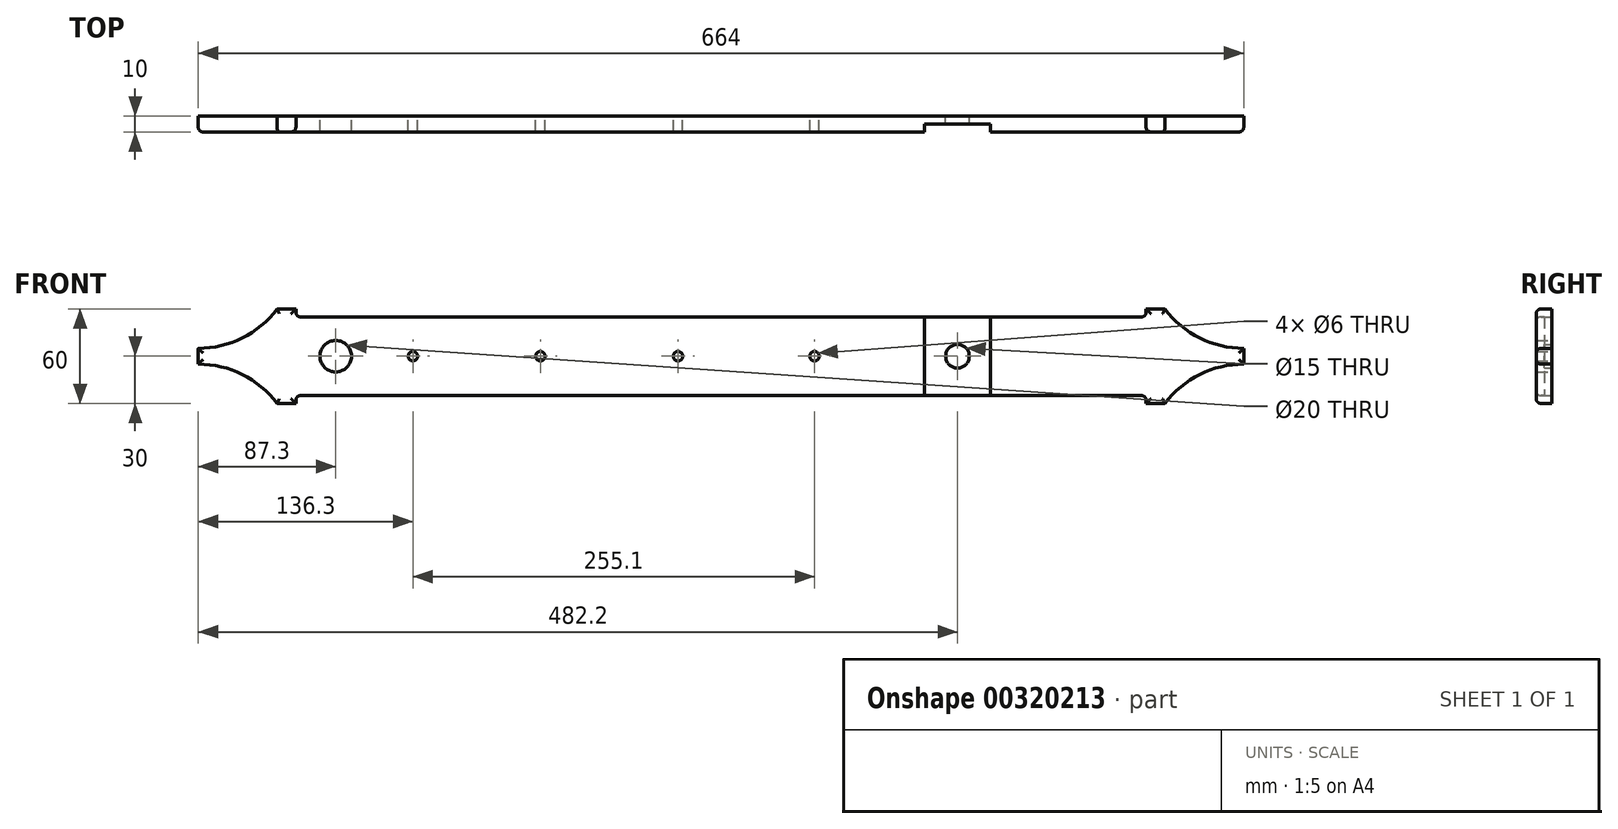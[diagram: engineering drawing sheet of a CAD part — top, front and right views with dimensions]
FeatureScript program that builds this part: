
annotation { "Feature Type Name" : "Feature", "Feature Type Description" : "" }
export const myFeature = defineFeature(function(context is Context, id is Id, definition is map)
    precondition{}
    {
        {
            var Q0;
            Q0=qCreatedBy(makeId("Front.planeOp"),FACE);
            var sketch = newSketch(context, id + "F0", { "sketchPlane" : qUnion([Q0])});
            skLineSegment(sketch, "E0", {"start": v(0, 0) * mm, "end": v(-664, 0) * mm, "construction": true});
            skLineSegment(sketch, "E1", {"start": v(0, 0) * mm, "end": v(0, 5) * mm});
            skLineSegment(sketch, "E2", {"start": v(-50, 30) * mm, "end": v(-62, 30) * mm});
            skArc(sketch, "E3", {"start": v(-50, 30) * mm, "mid": v(-27.95, 11.6) * mm, "end": v(0, 5) * mm});
            skLineSegment(sketch, "E4", {"start": v(-62, 30) * mm, "end": v(-62, 28) * mm});
            skLineSegment(sketch, "E5", {"start": v(-65, 25) * mm, "end": v(-332, 25) * mm});
            skLineSegment(sketch, "E6.MirrorCS", {"start": v(-599, 25) * mm, "end": v(-332, 25) * mm});
            skLineSegment(sketch, "E7.MirrorCS", {"start": v(-602, 30) * mm, "end": v(-602, 28) * mm});
            skLineSegment(sketch, "E8.MirrorCS", {"start": v(-614, 30) * mm, "end": v(-602, 30) * mm});
            skArc(sketch, "E9.MirrorCS", {"start": v(-614, 30) * mm, "mid": v(-636.05, 11.6) * mm, "end": v(-664, 5) * mm});
            skLineSegment(sketch, "E10.MirrorCS", {"start": v(-664, 0) * mm, "end": v(-664, 5) * mm});
            skLineSegment(sketch, "E11.MirrorCS", {"start": v(-664, 0) * mm, "end": v(-664, -5) * mm});
            skArc(sketch, "E12.MirrorCS", {"start": v(-614, -30) * mm, "mid": v(-636.05, -11.6) * mm, "end": v(-664, -5) * mm});
            skLineSegment(sketch, "E13.MirrorCS", {"start": v(-614, -30) * mm, "end": v(-602, -30) * mm});
            skLineSegment(sketch, "E14.MirrorCS", {"start": v(-602, -30) * mm, "end": v(-602, -28) * mm});
            skLineSegment(sketch, "E15.MirrorCS", {"start": v(-599, -25) * mm, "end": v(-332, -25) * mm});
            skLineSegment(sketch, "E16.MirrorCS", {"start": v(-65, -25) * mm, "end": v(-332, -25) * mm});
            skLineSegment(sketch, "E17.MirrorCS", {"start": v(-62, -30) * mm, "end": v(-62, -28) * mm});
            skLineSegment(sketch, "E18.MirrorCS", {"start": v(-50, -30) * mm, "end": v(-62, -30) * mm});
            skArc(sketch, "E19.MirrorCS", {"start": v(-50, -30) * mm, "mid": v(-27.95, -11.6) * mm, "end": v(0, -5) * mm});
            skLineSegment(sketch, "E20.MirrorCS", {"start": v(0, 0) * mm, "end": v(0, -5) * mm});
            skPoint(sketch, "E21.visualSharp", {"position": v(-62, 25) * mm});
            skArc(sketch, "E21.filletArc", {"start": v(-65, 25) * mm, "mid": v(-62.88, 25.88) * mm, "end": v(-62, 28) * mm});
            skPoint(sketch, "E22.visualSharp", {"position": v(-62, -25) * mm});
            skArc(sketch, "E22.filletArc", {"start": v(-62, -28) * mm, "mid": v(-62.88, -25.88) * mm, "end": v(-65, -25) * mm});
            skPoint(sketch, "E23.visualSharp", {"position": v(-602, 25) * mm});
            skArc(sketch, "E23.filletArc", {"start": v(-602, 28) * mm, "mid": v(-601.12, 25.88) * mm, "end": v(-599, 25) * mm});
            skPoint(sketch, "E24.visualSharp", {"position": v(-602, -25) * mm});
            skArc(sketch, "E24.filletArc", {"start": v(-599, -25) * mm, "mid": v(-601.12, -25.88) * mm, "end": v(-602, -28) * mm});
            skCircle(sketch, "E25", {"center": v(-576.7, 0) * mm, "radius": 10 * mm});
            skCircle(sketch, "E26", {"center": v(-527.7, 0) * mm, "radius": 3 * mm});
            skCircle(sketch, "E27", {"center": v(-446.7, 0) * mm, "radius": 3 * mm});
            skCircle(sketch, "E28", {"center": v(-359.3, 0) * mm, "radius": 3 * mm});
            skCircle(sketch, "E29", {"center": v(-272.6, 0) * mm, "radius": 3 * mm});
            skCircle(sketch, "E30", {"center": v(-181.8, 0) * mm, "radius": 7.5 * mm});
            skSolve(sketch);
        }
        {
            var Q0;
            Q0 = qSketchRegion(id + "F0", true);
            extrude(context, id + "F1", {"entities" : qUnion([Q0]), "depth" : 10 * mm});
        }
        {
            var Q0;
            Q0=makeQuery(id+"F1.opExtrude","CAP_FACE",FACE,{"disambiguationData":[OSD([sQuery(id+"F0.wireOp",EDGE,"E2"),sQuery(id+"F0.wireOp",EDGE,"E1"),sQuery(id+"F0.wireOp",EDGE,"E3"),sQuery(id+"F0.wireOp",EDGE,"E4"),sQuery(id+"F0.wireOp",EDGE,"E5"),sQuery(id+"F0.wireOp",EDGE,"E6.MirrorCS"),sQuery(id+"F0.wireOp",EDGE,"E7.MirrorCS"),sQuery(id+"F0.wireOp",EDGE,"E8.MirrorCS"),sQuery(id+"F0.wireOp",EDGE,"E10.MirrorCS"),sQuery(id+"F0.wireOp",EDGE,"E9.MirrorCS"),sQuery(id+"F0.wireOp",EDGE,"E11.MirrorCS"),sQuery(id+"F0.wireOp",EDGE,"E12.MirrorCS"),sQuery(id+"F0.wireOp",EDGE,"E13.MirrorCS"),sQuery(id+"F0.wireOp",EDGE,"E14.MirrorCS"),sQuery(id+"F0.wireOp",EDGE,"E15.MirrorCS"),sQuery(id+"F0.wireOp",EDGE,"E16.MirrorCS"),sQuery(id+"F0.wireOp",EDGE,"E17.MirrorCS"),sQuery(id+"F0.wireOp",EDGE,"E18.MirrorCS"),sQuery(id+"F0.wireOp",EDGE,"E19.MirrorCS"),sQuery(id+"F0.wireOp",EDGE,"E20.MirrorCS"),sQuery(id+"F0.wireOp",EDGE,"E21.filletArc"),sQuery(id+"F0.wireOp",EDGE,"E22.filletArc"),sQuery(id+"F0.wireOp",EDGE,"E23.filletArc"),sQuery(id+"F0.wireOp",EDGE,"E24.filletArc"),sQuery(id+"F0.wireOp",EDGE,"E25"),sQuery(id+"F0.wireOp",EDGE,"E26"),sQuery(id+"F0.wireOp",EDGE,"E27"),sQuery(id+"F0.wireOp",EDGE,"E28"),sQuery(id+"F0.wireOp",EDGE,"E29"),sQuery(id+"F0.wireOp",EDGE,"E30")])],"isStart":false});
            var sketch = newSketch(context, id + "F2", { "sketchPlane" : qUnion([Q0])});
            skLineSegment(sketch, "E31", {"start": v(-160.8, 25) * mm, "end": v(-160.8, -25) * mm});
            skLineSegment(sketch, "E32", {"start": v(-202.8, 25) * mm, "end": v(-202.8, -25) * mm});
            skSolve(sketch);
        }
        {
            var Q0;
            Q0 = qSketchRegion(id + "F2", true);
            var Q1;
            {var subQ0=sQuery(id+"F2.wireOp",EDGE,"E31");Q1=makeQuery(id+"F2.imprint","IMPRINT",FACE,{"disambiguationData":[TD([[makeQuery(id+"F2.imprint","IMPRINT",EDGE,{"derivedFrom":subQ0}),-1.0]])]});}
            extrude(context, id + "F3", {"entities" : qUnion([Q0, Q1]), "operationType" : NewBodyOperationType.REMOVE, "oppositeDirection" : true, "depth" : 5 * mm});
        }
        {
            var Q0;
            {var subQ0=sQuery(id+"F0.wireOp",EDGE,"E23.filletArc");var subQ1=sQuery(id+"F0.wireOp",EDGE,"E6.MirrorCS");var subQ2=sQuery(id+"F0.wireOp",EDGE,"E5");Q0=makeQuery(id+"F3.boolean.opBoolean","SPLIT",EDGE,{"disambiguationData":[TD([makeQuery(id+"F1.opExtrude","SWEPT_FACE",FACE,{"disambiguationData":[OSD([subQ0])]})])],"derivedFrom":makeQuery(id+"F1.opExtrude","CAP_EDGE",EDGE,{"disambiguationData":[OSD([subQ2,subQ1])],"isStart":false})});}
            var Q1;
            {var subQ0=sQuery(id+"F0.wireOp",EDGE,"E24.filletArc");var subQ1=sQuery(id+"F0.wireOp",EDGE,"E16.MirrorCS");var subQ2=sQuery(id+"F0.wireOp",EDGE,"E15.MirrorCS");Q1=makeQuery(id+"F3.boolean.opBoolean","SPLIT",EDGE,{"disambiguationData":[TD([makeQuery(id+"F1.opExtrude","SWEPT_FACE",FACE,{"disambiguationData":[OSD([subQ0])]})])],"derivedFrom":makeQuery(id+"F1.opExtrude","CAP_EDGE",EDGE,{"disambiguationData":[OSD([subQ2,subQ1])],"isStart":false})});}
            var Q2;
            {var subQ0=sQuery(id+"F0.wireOp",EDGE,"E22.filletArc");var subQ1=sQuery(id+"F0.wireOp",EDGE,"E16.MirrorCS");var subQ2=sQuery(id+"F0.wireOp",EDGE,"E15.MirrorCS");Q2=makeQuery(id+"F3.boolean.opBoolean","SPLIT",EDGE,{"disambiguationData":[TD([makeQuery(id+"F1.opExtrude","SWEPT_FACE",FACE,{"disambiguationData":[OSD([subQ0])]})])],"derivedFrom":makeQuery(id+"F1.opExtrude","CAP_EDGE",EDGE,{"disambiguationData":[OSD([subQ2,subQ1])],"isStart":false})});}
            var Q3;
            {var subQ0=sQuery(id+"F0.wireOp",EDGE,"E21.filletArc");var subQ1=sQuery(id+"F0.wireOp",EDGE,"E6.MirrorCS");var subQ2=sQuery(id+"F0.wireOp",EDGE,"E5");Q3=makeQuery(id+"F3.boolean.opBoolean","SPLIT",EDGE,{"disambiguationData":[TD([makeQuery(id+"F1.opExtrude","SWEPT_FACE",FACE,{"disambiguationData":[OSD([subQ0])]})])],"derivedFrom":makeQuery(id+"F1.opExtrude","CAP_EDGE",EDGE,{"disambiguationData":[OSD([subQ2,subQ1])],"isStart":false})});}
            var Q4;
            Q4=makeQuery(id+"F1.opExtrude","CAP_EDGE",EDGE,{"disambiguationData":[OSD([sQuery(id+"F0.wireOp",EDGE,"E18.MirrorCS")])],"isStart":false});
            var Q5;
            Q5=makeQuery(id+"F1.opExtrude","CAP_EDGE",EDGE,{"disambiguationData":[OSD([sQuery(id+"F0.wireOp",EDGE,"E19.MirrorCS")])],"isStart":false});
            var Q6;
            Q6=makeQuery(id+"F1.opExtrude","CAP_EDGE",EDGE,{"disambiguationData":[OSD([sQuery(id+"F0.wireOp",EDGE,"E1"),sQuery(id+"F0.wireOp",EDGE,"E20.MirrorCS")])],"isStart":false});
            var Q7;
            Q7=makeQuery(id+"F1.opExtrude","CAP_EDGE",EDGE,{"disambiguationData":[OSD([sQuery(id+"F0.wireOp",EDGE,"E3")])],"isStart":false});
            var Q8;
            Q8=makeQuery(id+"F1.opExtrude","CAP_EDGE",EDGE,{"disambiguationData":[OSD([sQuery(id+"F0.wireOp",EDGE,"E2")])],"isStart":false});
            var Q9;
            Q9=makeQuery(id+"F1.opExtrude","CAP_EDGE",EDGE,{"disambiguationData":[OSD([sQuery(id+"F0.wireOp",EDGE,"E13.MirrorCS")])],"isStart":false});
            var Q10;
            Q10=makeQuery(id+"F1.opExtrude","CAP_EDGE",EDGE,{"disambiguationData":[OSD([sQuery(id+"F0.wireOp",EDGE,"E12.MirrorCS")])],"isStart":false});
            var Q11;
            Q11=makeQuery(id+"F1.opExtrude","CAP_EDGE",EDGE,{"disambiguationData":[OSD([sQuery(id+"F0.wireOp",EDGE,"E10.MirrorCS"),sQuery(id+"F0.wireOp",EDGE,"E11.MirrorCS")])],"isStart":false});
            var Q12;
            Q12=makeQuery(id+"F1.opExtrude","CAP_EDGE",EDGE,{"disambiguationData":[OSD([sQuery(id+"F0.wireOp",EDGE,"E9.MirrorCS")])],"isStart":false});
            var Q13;
            Q13=makeQuery(id+"F1.opExtrude","CAP_EDGE",EDGE,{"disambiguationData":[OSD([sQuery(id+"F0.wireOp",EDGE,"E8.MirrorCS")])],"isStart":false});
            fillet(context, id + "F4", {"entities" : qUnion([Q0, Q1, Q2, Q3, Q4, Q5, Q6, Q7, Q8, Q9, Q10, Q11, Q12, Q13]), "radius" : 3 * mm, "tangentPropagation" : true, "allowEdgeOverflow" : false});
        }
    });
